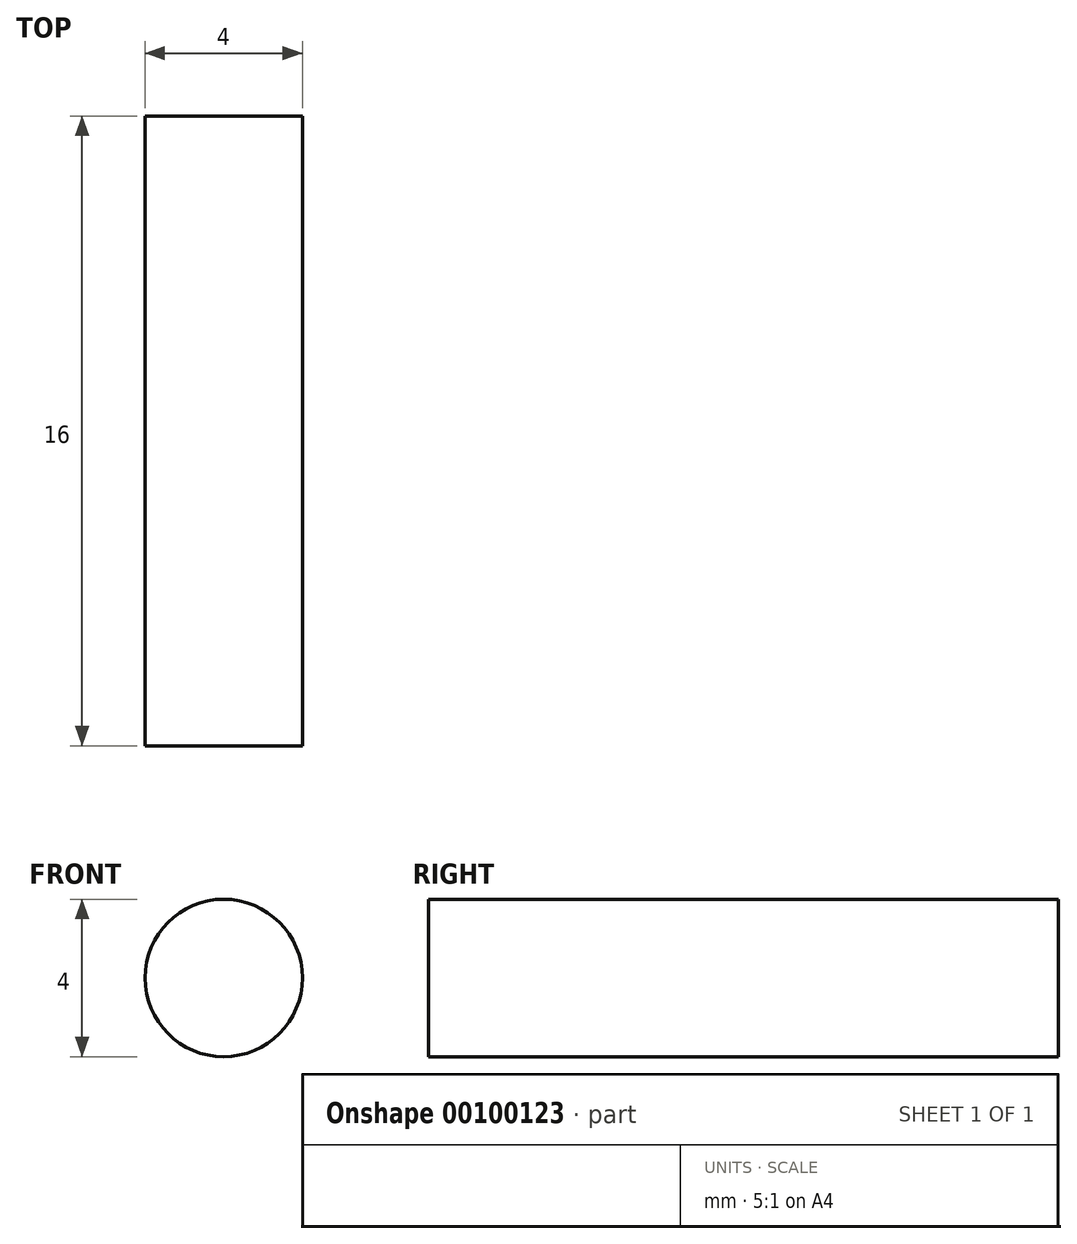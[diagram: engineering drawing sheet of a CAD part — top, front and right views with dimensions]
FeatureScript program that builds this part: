
annotation { "Feature Type Name" : "Feature", "Feature Type Description" : "" }
export const myFeature = defineFeature(function(context is Context, id is Id, definition is map)
    precondition{}
    {
        {
            var Q0;
            Q0=qCreatedBy(makeId("Front.planeOp"),FACE);
            var sketch = newSketch(context, id + "F0", { "sketchPlane" : qUnion([Q0])});
            skCircle(sketch, "E0", {"center": v(0, 0) * mm, "radius": 2 * mm});
            skSolve(sketch);
        }
        {
            var Q0;
            Q0=makeQuery(id+"F0.imprint","IMPRINT",FACE,{"disambiguationData":[TD([[makeQuery(id+"F0.imprint","IMPRINT",EDGE,{"derivedFrom":sQuery(id+"F0.wireOp",EDGE,"E0")}),1.0]])]});
            extrude(context, id + "F1", {"entities" : qUnion([Q0]), "depth" : 16 * mm});
        }
    });
